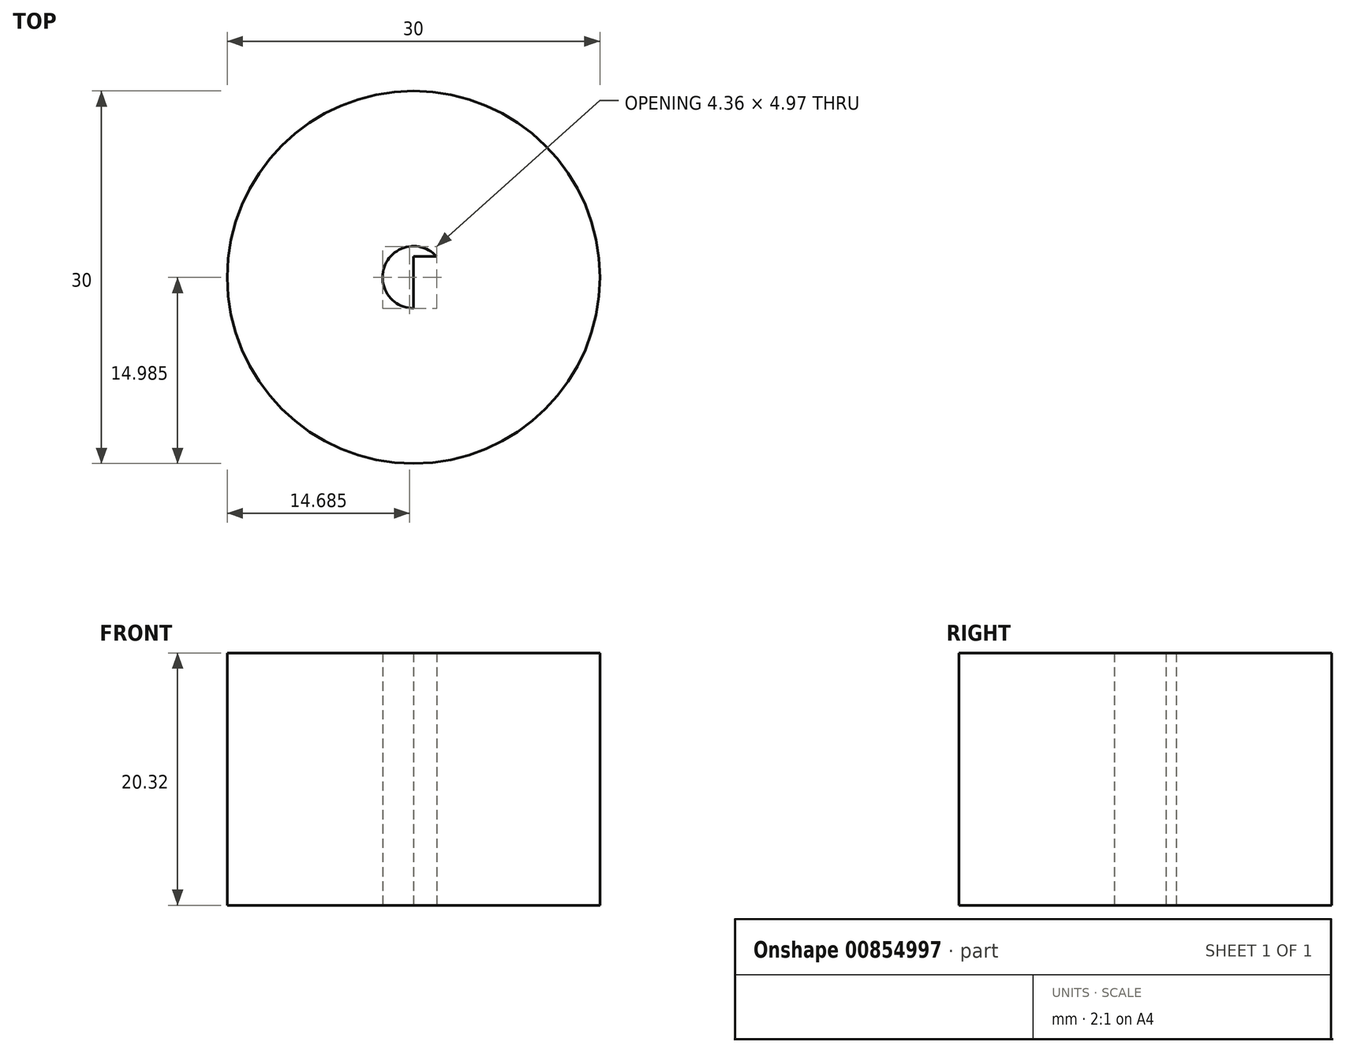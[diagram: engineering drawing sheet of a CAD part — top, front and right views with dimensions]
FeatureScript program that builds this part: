
annotation { "Feature Type Name" : "Feature", "Feature Type Description" : "" }
export const myFeature = defineFeature(function(context is Context, id is Id, definition is map)
    precondition{}
    {
        {
            var Q0;
            Q0=qCreatedBy(makeId("Top.planeOp"),FACE);
            var sketch = newSketch(context, id + "F0", { "sketchPlane" : qUnion([Q0])});
            skCircle(sketch, "E0", {"center": v(0, 0) * mm, "radius": 2.5 * mm});
            skCircle(sketch, "E1", {"center": v(0, 0) * mm, "radius": 15 * mm});
            skLineSegment(sketch, "E2", {"start": v(0, -2.5) * mm, "end": v(0, 1.67) * mm});
            skLineSegment(sketch, "E3", {"start": v(0, 1.67) * mm, "end": v(-1.86, 1.67) * mm});
            skLineSegment(sketch, "E4", {"start": v(-1.86, 1.67) * mm, "end": v(1.86, 1.67) * mm});
            skSolve(sketch);
        }
        {
            var Q0;
            Q0=makeQuery(id+"F0.imprint","IMPRINT",FACE,{"disambiguationData":[TD([[makeQuery(id+"F0.imprint","IMPRINT",EDGE,{"derivedFrom":sQuery(id+"F0.wireOp",EDGE,"E0")}),-1.0]])]});
            extrude(context, id + "F1", {"entities" : qUnion([Q0]), "depth" : 20.32 * mm, "offsetDistance" : 25.4 * mm});
        }
        {
            var Q0;
            {var subQ0=sQuery(id+"F0.wireOp",EDGE,"E4");var subQ1=sQuery(id+"F0.wireOp",EDGE,"E0");var subQ2=makeQuery(id+"F0.imprint","INTERSECT",VERTEX,{"disambiguationData":[OD(0.0)],"derivedFrom":[subQ1,subQ0]});Q0=makeQuery(id+"F0.imprint","IMPRINT",FACE,{"disambiguationData":[TD([[makeQuery(id+"F0.imprint","IMPRINT",EDGE,{"disambiguationData":[TD([[subQ2,1.0]])],"derivedFrom":subQ1}),1.0]])]});}
            extrude(context, id + "F2", {"entities" : qUnion([Q0]), "operationType" : NewBodyOperationType.ADD, "depth" : 20.32 * mm, "offsetDistance" : 25.4 * mm});
        }
    });
